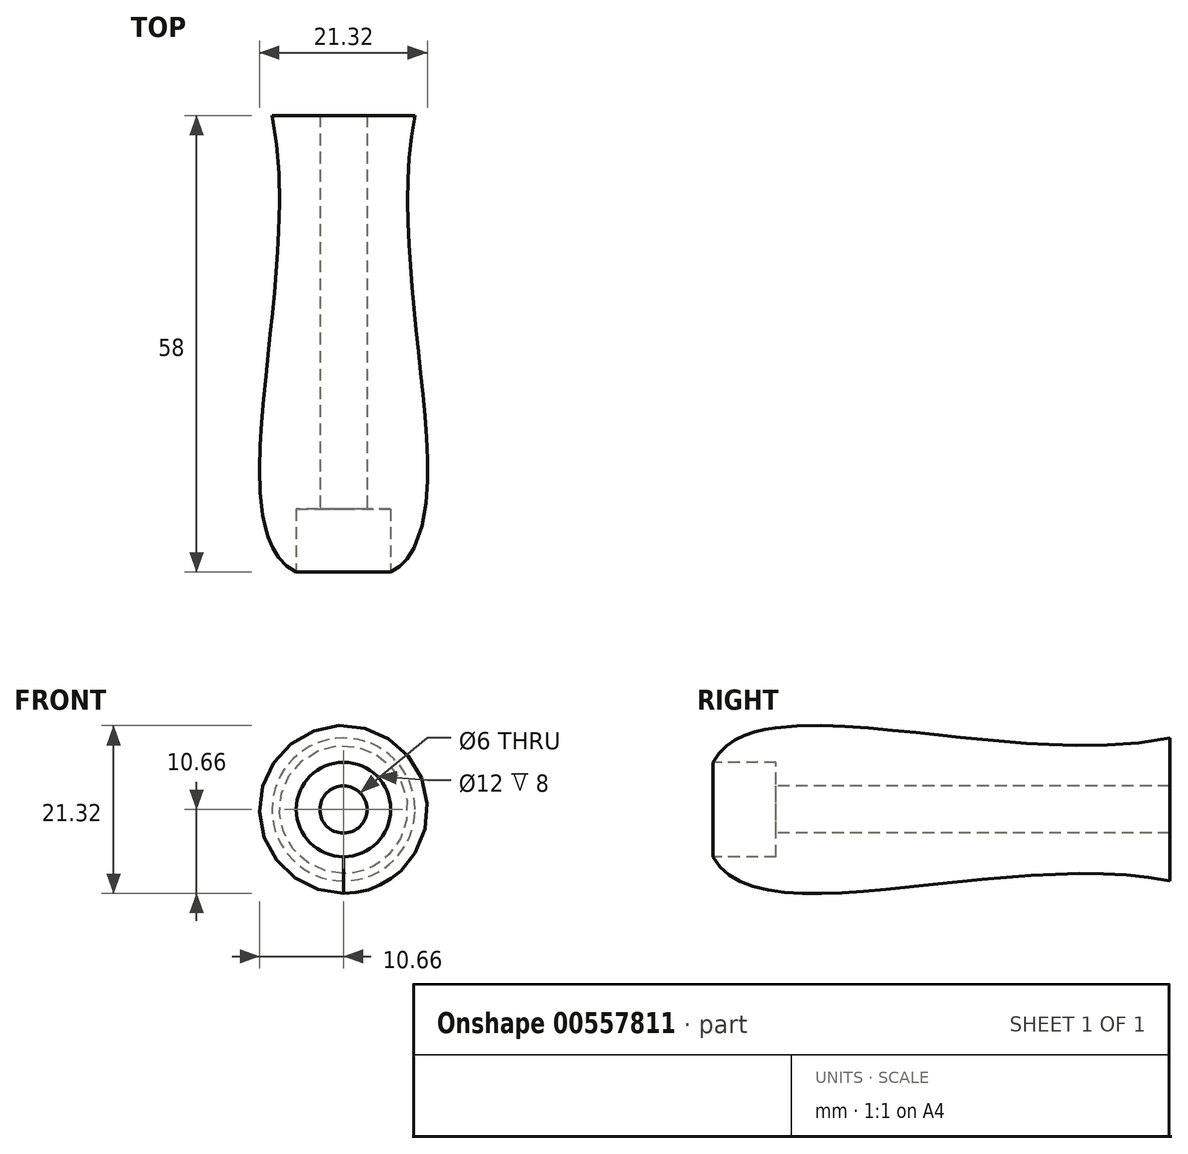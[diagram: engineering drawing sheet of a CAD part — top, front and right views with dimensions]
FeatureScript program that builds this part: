
annotation { "Feature Type Name" : "Feature", "Feature Type Description" : "" }
export const myFeature = defineFeature(function(context is Context, id is Id, definition is map)
    precondition{}
    {
        {
            var Q0;
            Q0=qCreatedBy(makeId("Right.planeOp"),FACE);
            var sketch = newSketch(context, id + "F0", { "sketchPlane" : qUnion([Q0])});
            skLineSegment(sketch, "E0", {"start": v(0, 3) * mm, "end": v(-50, 3) * mm});
            skLineSegment(sketch, "E1", {"start": v(-50, 3) * mm, "end": v(-50, 6) * mm});
            skLineSegment(sketch, "E2", {"start": v(-50, 6) * mm, "end": v(-58, 6) * mm});
            skLineSegment(sketch, "E3", {"start": v(0, 3) * mm, "end": v(0, 9.08) * mm});
            skFitSpline(sketch, "E4", {"points": [v(0, 9.08) * mm, v(-58, 6) * mm], "startDerivative": vector(-60.82, -12.66) * mm, "endDerivative": vector(-16.22, -32.43) * mm});
            skLineSegment(sketch, "E5", {"start": v(-67.43, 0) * mm, "end": v(30.78, 0) * mm, "construction": true});
            skSolve(sketch);
        }
        {
            var Q0;
            Q0 = qSketchRegion(id + "F0", true);
            var Q1;
            Q1=sQuery(id+"F0.wireOp",EDGE,"E5");
            revolve(context, id + "F1", {"entities" : qUnion([Q0]), "axis" : qUnion([Q1]), "revolveType" : RevolveType.FULL});
        }
    });
